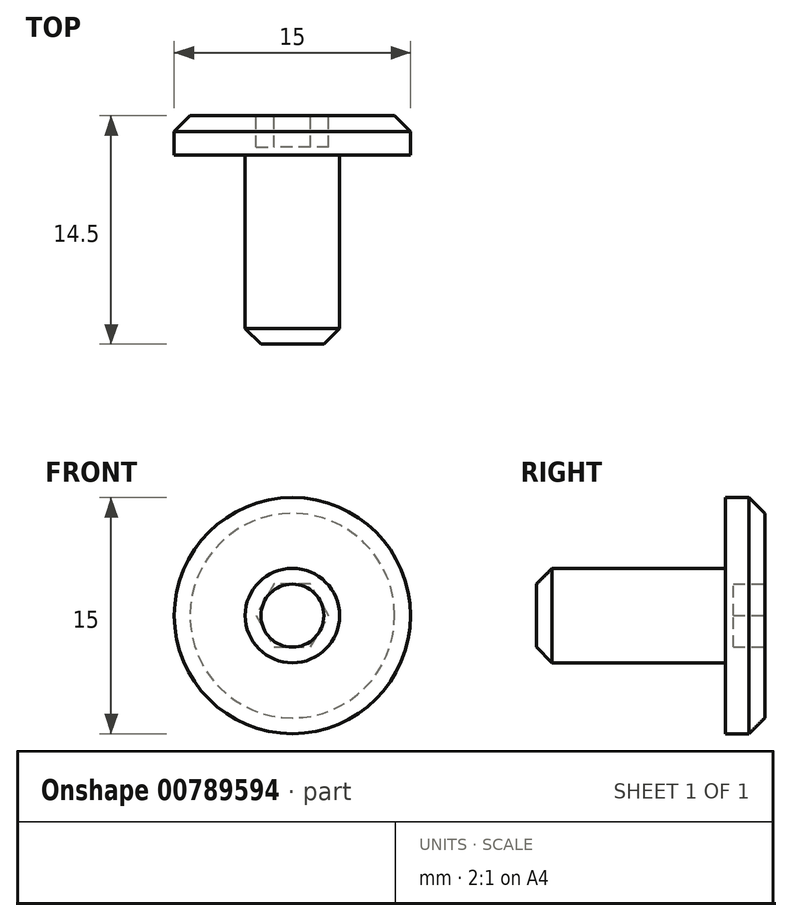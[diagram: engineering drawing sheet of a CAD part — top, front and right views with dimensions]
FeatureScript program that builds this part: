
annotation { "Feature Type Name" : "Feature", "Feature Type Description" : "" }
export const myFeature = defineFeature(function(context is Context, id is Id, definition is map)
    precondition{}
    {
        {
            var Q0;
            Q0=qCreatedBy(makeId("Top.planeOp"),FACE);
            var sketch = newSketch(context, id + "F0", { "sketchPlane" : qUnion([Q0])});
            skLineSegment(sketch, "E0", {"start": v(0, 0) * mm, "end": v(-3, 0) * mm});
            skLineSegment(sketch, "E1", {"start": v(-3, 0) * mm, "end": v(-3, 12) * mm});
            skLineSegment(sketch, "E2", {"start": v(-3, 12) * mm, "end": v(-7.5, 12) * mm});
            skLineSegment(sketch, "E3", {"start": v(-7.5, 12) * mm, "end": v(-7.5, 14.5) * mm});
            skLineSegment(sketch, "E4", {"start": v(-7.5, 14.5) * mm, "end": v(0, 14.5) * mm});
            skLineSegment(sketch, "E5", {"start": v(0, 14.5) * mm, "end": v(0, 0) * mm});
            skLineSegment(sketch, "E6", {"start": v(0, 14.5) * mm, "end": v(0, 18.07) * mm, "construction": true});
            skSolve(sketch);
        }
        {
            var Q0;
            Q0=makeQuery(id+"F0.imprint","IMPRINT",FACE,{"disambiguationData":[TD([[makeQuery(id+"F0.imprint","IMPRINT",EDGE,{"derivedFrom":sQuery(id+"F0.wireOp",EDGE,"E0")}),-1.0]])]});
            var Q1;
            Q1=sQuery(id+"F0.wireOp",EDGE,"E5");
            revolve(context, id + "F1", {"surfaceOperationType" : NewSurfaceOperationType.NEW, "entities" : qUnion([Q0]), "axis" : qUnion([Q1]), "revolveType" : RevolveType.FULL});
        }
        {
            var Q0;
            Q0=makeQuery(id+"F1.opRevolve","SWEPT_EDGE",EDGE,{"disambiguationData":[OSD([sQuery(id+"F0.wireOp",EDGE,"E3"),sQuery(id+"F0.wireOp",EDGE,"E4")])]});
            var Q1;
            Q1=makeQuery(id+"F1.opRevolve","SWEPT_EDGE",EDGE,{"disambiguationData":[OSD([sQuery(id+"F0.wireOp",EDGE,"E0"),sQuery(id+"F0.wireOp",EDGE,"E1")])]});
            chamfer(context, id + "F2", {"entities" : qUnion([Q0, Q1]), "width" : 1 * mm, "tangentPropagation" : true});
        }
        {
            var Q0;
            Q0=makeQuery(id+"F1.opRevolve","SWEPT_FACE",FACE,{"disambiguationData":[OSD([sQuery(id+"F0.wireOp",EDGE,"E4")])]});
            var sketch = newSketch(context, id + "F3", { "sketchPlane" : qUnion([Q0])});
            skCircle(sketch, "E7.cCircle", {"center": v(0, 0) * mm, "radius": 2 * mm, "construction": true});
            skLineSegment(sketch, "E7.0", {"start": v(-1.15, 2) * mm, "end": v(1.15, 2) * mm});
            skLineSegment(sketch, "E7.1", {"start": v(1.15, 2) * mm, "end": v(2.3, 0) * mm});
            skLineSegment(sketch, "E7.2", {"start": v(2.3, 0) * mm, "end": v(1.15, -2) * mm});
            skLineSegment(sketch, "E7.3", {"start": v(1.15, -2) * mm, "end": v(-1.15, -2) * mm});
            skLineSegment(sketch, "E7.4", {"start": v(-1.15, -2) * mm, "end": v(-2.3, 0) * mm});
            skLineSegment(sketch, "E7.5", {"start": v(-2.3, 0) * mm, "end": v(-1.15, 2) * mm});
            skPoint(sketch, "E7.0.midPoint", {"position": v(0, 2) * mm});
            skSolve(sketch);
        }
        {
            var Q0;
            Q0 = qSketchRegion(id + "F3", true);
            extrude(context, id + "F4", {"entities" : qUnion([Q0]), "operationType" : NewBodyOperationType.REMOVE, "oppositeDirection" : true, "depth" : 2 * mm, "offsetDistance" : 25 * mm});
        }
    });
